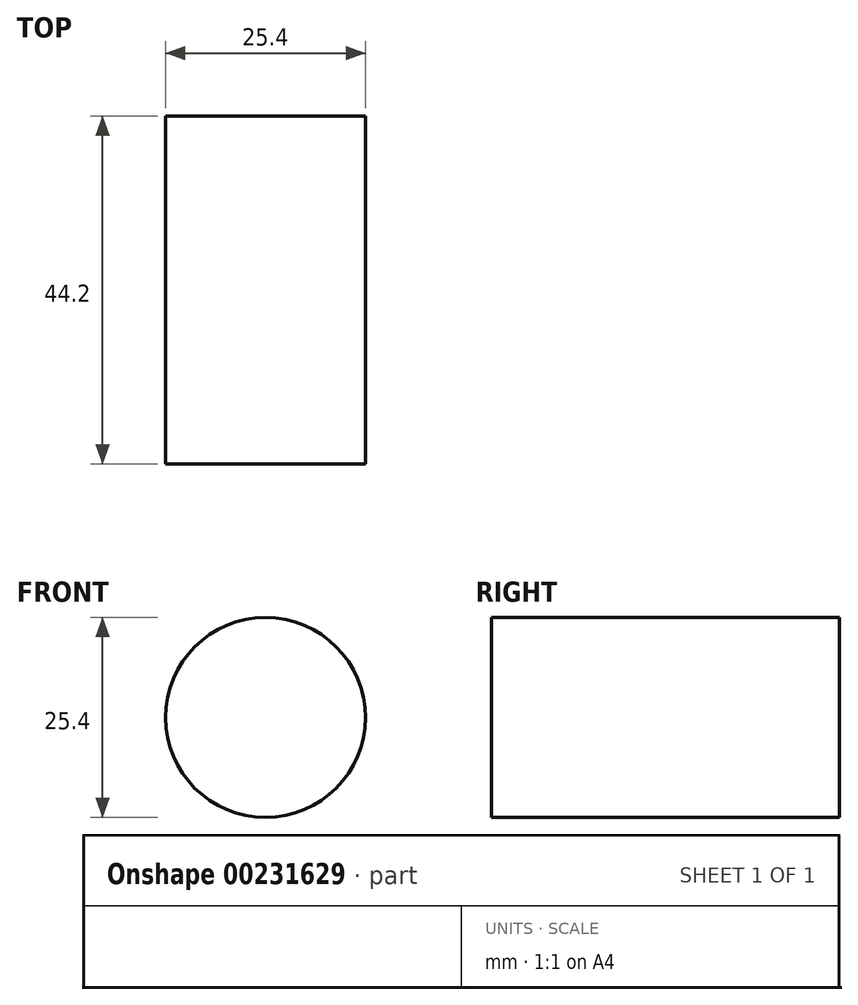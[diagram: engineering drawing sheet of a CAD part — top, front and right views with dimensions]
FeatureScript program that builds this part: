
annotation { "Feature Type Name" : "Feature", "Feature Type Description" : "" }
export const myFeature = defineFeature(function(context is Context, id is Id, definition is map)
    precondition{}
    {
        {
            var Q0;
            Q0=qCreatedBy(makeId("Front.planeOp"),FACE);
            var sketch = newSketch(context, id + "F0", { "sketchPlane" : qUnion([Q0])});
            skCircle(sketch, "E0", {"center": v(-56.06, 48.57) * mm, "radius": 12.7 * mm});
            skSolve(sketch);
        }
        {
            var Q0;
            Q0 = qSketchRegion(id + "F0", true);
            extrude(context, id + "F1", {"entities" : qUnion([Q0]), "depth" : 44.2 * mm});
        }
    });
